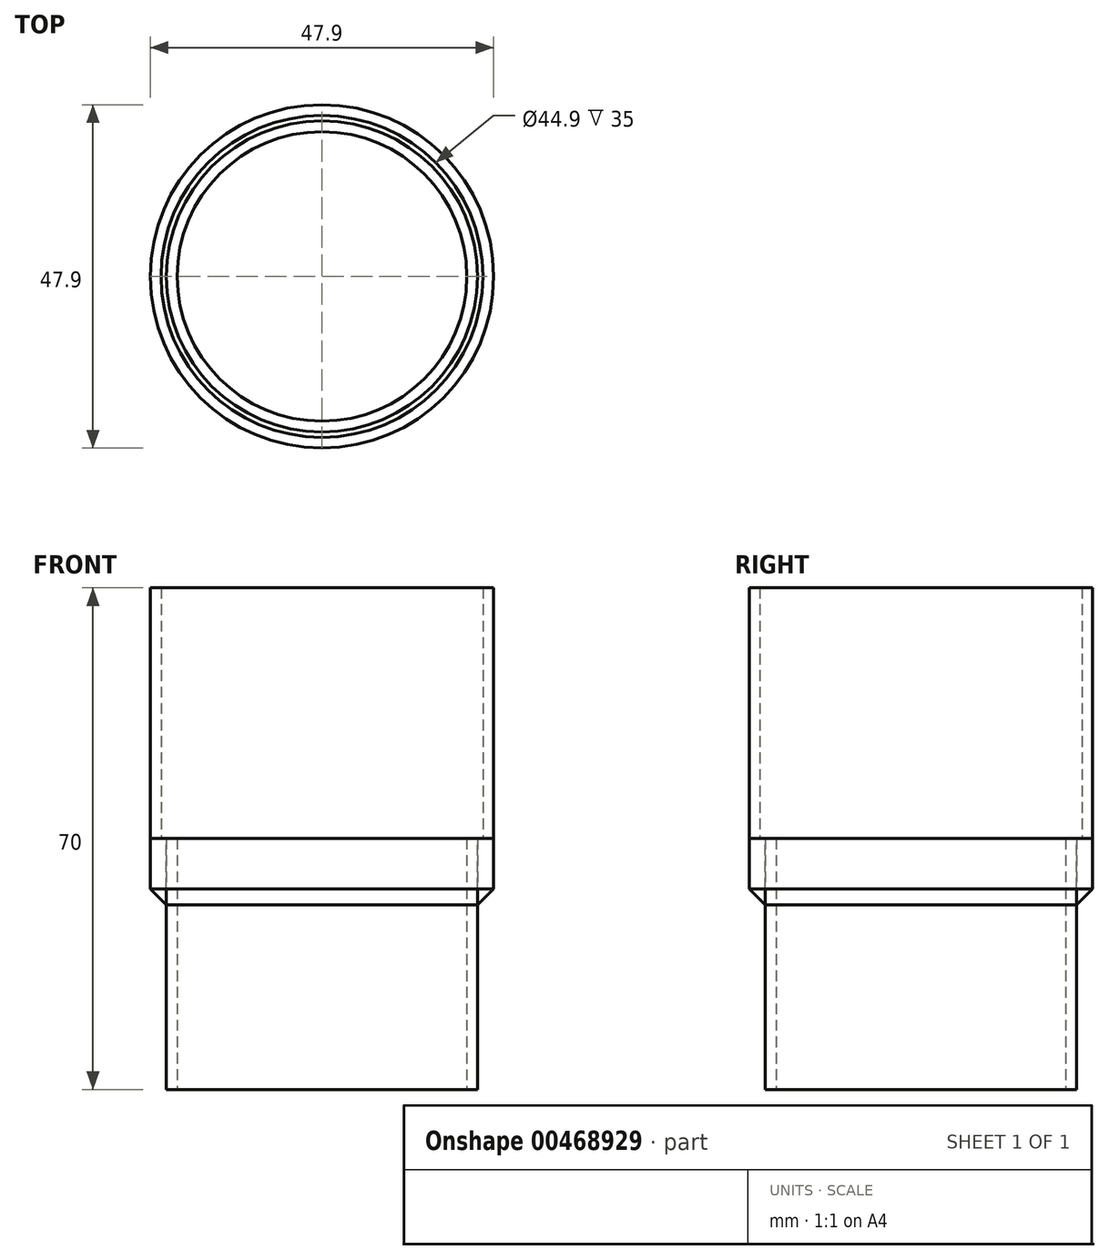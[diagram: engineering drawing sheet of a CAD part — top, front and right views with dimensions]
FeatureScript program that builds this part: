
annotation { "Feature Type Name" : "Feature", "Feature Type Description" : "" }
export const myFeature = defineFeature(function(context is Context, id is Id, definition is map)
    precondition{}
    {
        {
            var Q0;
            Q0=qCreatedBy(makeId("Top.planeOp"),FACE);
            var sketch = newSketch(context, id + "F0", { "sketchPlane" : qUnion([Q0])});
            skCircle(sketch, "E0", {"center": v(0, 0) * mm, "radius": 20.2 * mm});
            skCircle(sketch, "E1", {"center": v(0, 0) * mm, "radius": 21.7 * mm});
            skSolve(sketch);
        }
        {
            var Q0;
            Q0 = qSketchRegion(id + "F0", true);
            extrude(context, id + "F1", {"entities" : qUnion([Q0]), "depth" : 35 * mm});
        }
        {
            var Q0;
            Q0=makeQuery(id+"F1.opExtrude","CAP_FACE",FACE,{"disambiguationData":[OSD([sQuery(id+"F0.wireOp",EDGE,"E0"),sQuery(id+"F0.wireOp",EDGE,"E1")])],"isStart":false});
            var sketch = newSketch(context, id + "F2", { "sketchPlane" : qUnion([Q0])});
            skCircle(sketch, "E2", {"center": v(0, 0) * mm, "radius": 22.45 * mm});
            skCircle(sketch, "E3", {"center": v(0, 0) * mm, "radius": 23.95 * mm});
            skSolve(sketch);
        }
        {
            var Q0;
            Q0 = qSketchRegion(id + "F2", true);
            extrude(context, id + "F3", {"entities" : qUnion([Q0]), "depth" : 35 * mm});
        }
        {
            var Q0;
            Q0=makeQuery(id+"F3.opExtrude","CAP_FACE",FACE,{"disambiguationData":[OSD([sQuery(id+"F2.wireOp",EDGE,"E2"),sQuery(id+"F2.wireOp",EDGE,"E3")])],"isStart":true});
            var sketch = newSketch(context, id + "F4", { "sketchPlane" : qUnion([Q0])});
            skCircle(sketch, "E4", {"center": v(0, 0) * mm, "radius": 21.7 * mm});
            skCircle(sketch, "E5", {"center": v(0, 0) * mm, "radius": 23.95 * mm});
            skSolve(sketch);
        }
        {
            var Q0;
            Q0 = qSketchRegion(id + "F4", true);
            extrude(context, id + "F5", {"entities" : qUnion([Q0]), "depth" : 10 * mm});
        }
        {
            var Q0;
            Q0=makeQuery(id+"F5.opExtrude","CAP_EDGE",EDGE,{"disambiguationData":[OSD([sQuery(id+"F4.wireOp",EDGE,"E5")])],"isStart":false});
            chamfer(context, id + "F6", {"entities" : qUnion([Q0]), "width" : 3 * mm, "tangentPropagation" : true});
        }
    });
